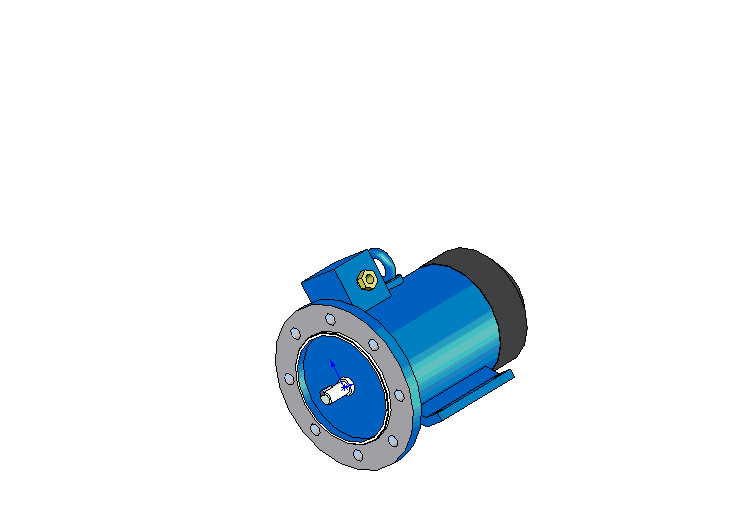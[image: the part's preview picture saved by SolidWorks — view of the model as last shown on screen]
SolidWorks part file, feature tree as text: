
SOLIDWORKS PART (.sldprt)
format: sldprt  version: not decoded by parser v0  size: 552,448 bytes
history: native  units: mm
features: sketch x18, extrude x13, plane x5, chamfer x4, cut_extrude x3, material x1, sweep x1 (+10 scaffold rows collapsed)
feature tree (55):
  scaffold x10  (default folders/planes/origin — collapsed)
  material  "Ст.3 ГОСТ 380-88"
  plane  "Спереди"
  plane  "Сверху"
  plane  "Справа"
  sketch  "Эскиз1"  dims[D1=11.0mm]
  extrude  "Вытянуть1"  Depth=23mm
  sketch  "Эскиз2"  dims[D1=4.0mm D2=4.0mm D3=1.5mm]
  extrude  "Вытянуть2"  Depth=10mm
  sketch  "Эскиз3"  dims[D1=15.0mm]
  extrude  "Вытянуть11"  Depth=4mm
  sketch  "Эскиз16"  dims[D1=95.0mm D2=140.0mm]
  extrude  "Вытянуть13"  Depth=10mm
  sketch  "Эскиз17"  dims[D1=95.0mm]
  extrude  "Вытянуть14"  Depth=23mm
  sketch  "Эскиз18"  dims[c1.D2=10.0mm c1.D1=~76.709708mm c2.D1=22.5deg c2.D3=57.5mm c2.D4=57.5mm c2.D5=57.5mm]
  cut_extrude  "Вырез-Вытянуть4"  [1 undecoded]
  sketch  "Эскиз20"  dims[D1=98.0mm]
  extrude  "Вытянуть15"  Depth=102mm
  sketch  "Эскиз21"  dims[D1=99.0mm]
  extrude  "Вытянуть16"  Depth=51mm
  chamfer  "Фаска3"  Distance=19.5mm Angle=45deg
  sketch  "Эскиз22"  dims[c1.D1=56.0mm c1.D2=~20.123009mm c2.D2=45.0deg c2.D3=~80.117559mm c3.D3=45.0deg c3.D4=~16.581424mm c4.D4=~178.814641deg c5.D4=7.0mm c5.D5=~8.201267mm c5.D6=7.0mm c5.D7=7.0mm c5.D8=106.0mm c5.D9=53.0mm c5.D10=74.0mm c5.D11=~66.502162mm c5.D12=~32.751236mm c5.D13=~35.619033mm c5.D14=~37.526152mm c5.D15=~37.387667mm]
  extrude  "Вытянуть17"  Depth=87mm
  sketch  "Эскиз23"  dims[c1.D3=5.8mm c1.D6=5.8mm c1.D7=5.8mm c1.D8=5.8mm c1.D9=5.8mm c1.D1=59.0mm c1.D2=71.0mm c2.D3=~9.532662mm c2.D4=45.0mm c2.D5=90.0deg c2.D6=71.0mm c2.D7=90.0mm c2.D8=90.0mm c2.D9=8.0mm c2.D10=59.0mm]
  cut_extrude  "Вырез-Вытянуть5"  [1 undecoded]
  plane  "Плоскость1"  Offset=42mm
  sketch  "Эскиз24"  dims[D1=42.0mm D2=42.0mm D3=40.0mm D4=~40.885628mm]
  extrude  "Вытянуть18"  Depth=43mm
  sketch  "Эскиз25"  dims[D1=25.0mm D2=88.0mm]
  extrude  "Вытянуть19"  Depth=12mm
  chamfer  "Фаска4"  Distance=1mm Angle=45deg
  plane  "Плоскость2"  Offset=88mm
  sketch  "Эскиз26"  dims[D1=24.0mm]
  sketch  "Эскиз27"  dims[c1.D1=2.0mm c1.D2=8.0mm c2.D1=24.0mm c2.D2=88.0mm]
  sweep  "По траектории1"
  chamfer  "Фаска5"  Distance=1mm Angle=45deg
  sketch  "Эскиз28"  dims[D1=90.0mm D2=95.0mm]
  extrude  "Вытянуть20"  Depth=7mm
  chamfer  "Фаска6"  Distance=0.5mm Angle=45deg
  sketch  "Эскиз29"  dims[D3=12.0mm D1=20.0mm D2=20.0mm]
  extrude  "Вытянуть21"  Depth=3mm
  sketch  "Эскиз30"  dims[D1=14.0mm]
  extrude  "Вытянуть22"  Depth=6mm
  sketch  "Эскиз31"  dims[D1=8.0mm D2=20.0mm D3=20.0mm]
  cut_extrude  "Вырез-Вытянуть6"  Depth=10mm
decode coverage: 36 of 39 modeling features carry decoded parameters
note: ~ marks probable driven/reference dimensions
note: 2 parameter values undecoded
note: suppression state not decoded; provenance and decode notes live in map.json
